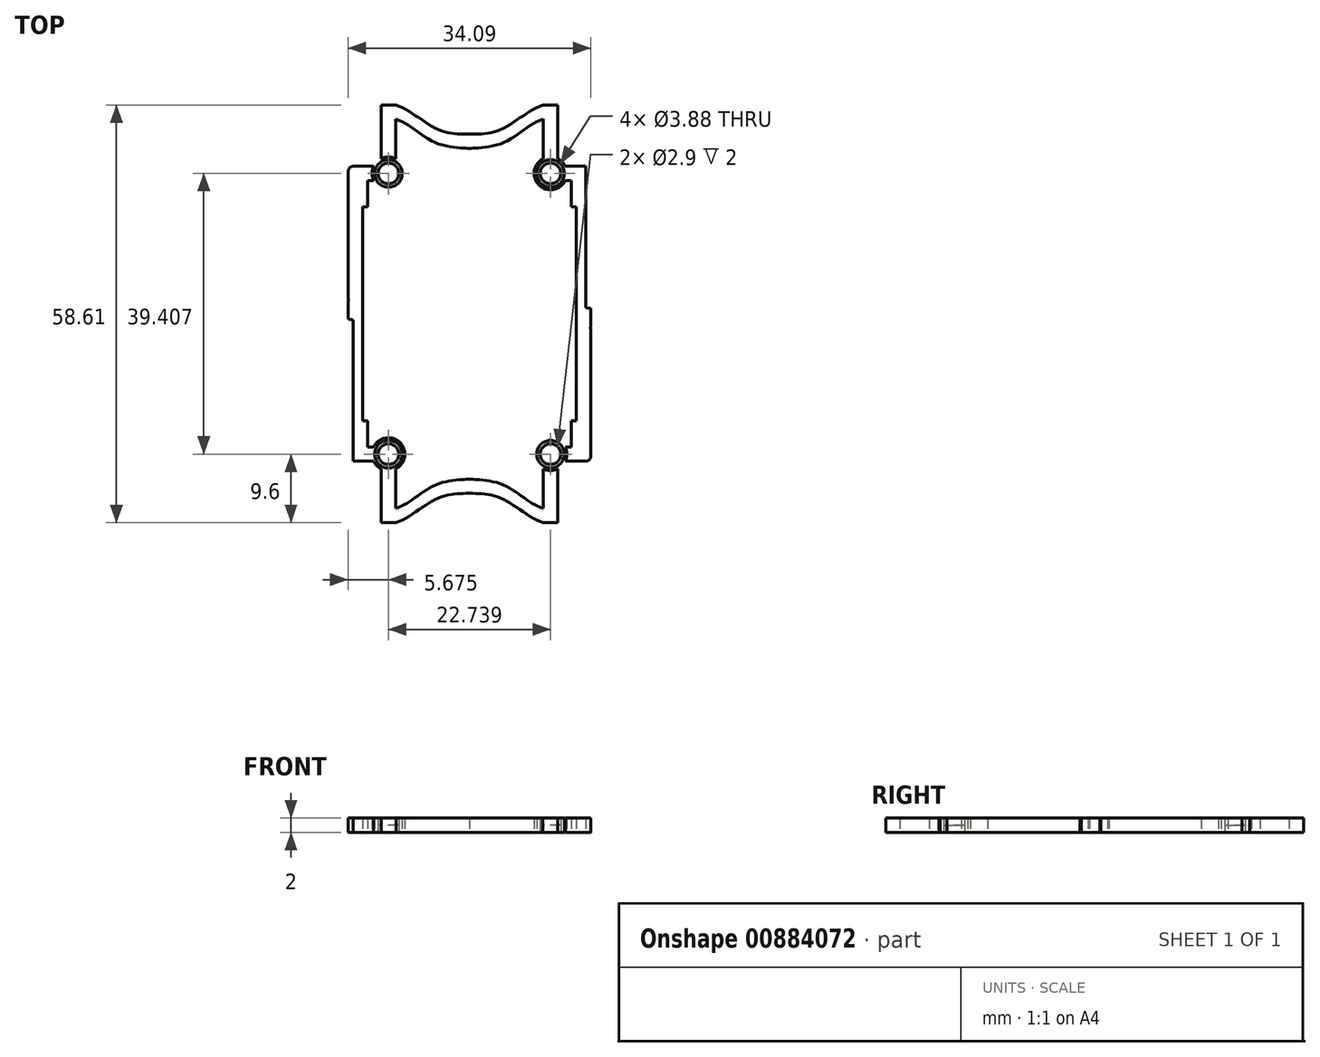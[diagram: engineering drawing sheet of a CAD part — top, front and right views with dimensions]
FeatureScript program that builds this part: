
annotation { "Feature Type Name" : "Feature", "Feature Type Description" : "" }
export const myFeature = defineFeature(function(context is Context, id is Id, definition is map)
    precondition{}
    {
        {
            var Q0;
            Q0=qCreatedBy(makeId("Right.planeOp"),FACE);
            cPlane(context, id + "F0", {"entities" : qUnion([Q0]), "cplaneType" : CPlaneType.OFFSET, "offset" : 33.58 * mm, "width" : 150 * mm, "height" : 150 * mm});
        }
        {
            var Q0;
            Q0=qCreatedBy(makeId("Top.planeOp"),FACE);
            var sketch = newSketch(context, id + "F1", { "sketchPlane" : qUnion([Q0])});
            skLineSegment(sketch, "E0.bottom", {"start": v(17.3, 63.43) * mm, "end": v(23.3, 63.43) * mm});
            skLineSegment(sketch, "E0.top", {"start": v(20.3, 4.82) * mm, "end": v(23.3, 4.82) * mm});
            skLineSegment(sketch, "E0.left", {"start": v(17.3, 63.43) * mm, "end": v(17.3, 38.95) * mm});
            skFitSpline(sketch, "E1", {"points": [v(49.88, 63.43) * mm, v(43.88, 63.43) * mm, v(38.18, 60.08) * mm, v(33.58, 59.34) * mm], "startDerivative": vector(-19.72, 0) * mm, "endDerivative": vector(-14.92, -0.07) * mm});
            skFitSpline(sketch, "E2.MirrorCS", {"points": [v(17.3, 63.43) * mm, v(23.3, 63.43) * mm, v(28.98, 60.08) * mm, v(33.58, 59.34) * mm], "startDerivative": vector(19.72, 0) * mm, "endDerivative": vector(14.92, -0.07) * mm});
            skFitSpline(sketch, "E3.MirrorCS", {"points": [v(49.88, 4.82) * mm, v(43.88, 4.82) * mm, v(38.18, 8.17) * mm, v(33.58, 8.91) * mm], "startDerivative": vector(-19.72, 0) * mm, "endDerivative": vector(-14.92, 0.07) * mm});
            skFitSpline(sketch, "E4.MirrorCS", {"points": [v(17.3, 4.82) * mm, v(23.3, 4.82) * mm, v(28.98, 8.17) * mm, v(33.58, 8.91) * mm], "startDerivative": vector(19.72, 0) * mm, "endDerivative": vector(14.92, 0.07) * mm});
            skLineSegment(sketch, "E5.trimOffspring", {"start": v(43.88, 63.43) * mm, "end": v(49.88, 63.43) * mm});
            skLineSegment(sketch, "E6.trimOffspring", {"start": v(43.88, 4.82) * mm, "end": v(49.88, 4.82) * mm});
            skArc(sketch, "E7.filletArc", {"start": v(17.3, 7.82) * mm, "mid": v(18.17, 5.7) * mm, "end": v(20.3, 4.82) * mm});
            skArc(sketch, "E8.MirrorCS", {"start": v(49.88, 7.82) * mm, "mid": v(49, 5.7) * mm, "end": v(46.88, 4.82) * mm});
            skArc(sketch, "E9.MirrorCS", {"start": v(49.88, 60.43) * mm, "mid": v(49, 62.55) * mm, "end": v(46.88, 63.43) * mm});
            skArc(sketch, "E10.MirrorCS", {"start": v(17.3, 60.43) * mm, "mid": v(18.17, 62.55) * mm, "end": v(20.3, 63.43) * mm});
            skCircle(sketch, "E11", {"center": v(22.21, 53.83) * mm, "radius": 1.45 * mm});
            skFitSpline(sketch, "E12", {"points": [v(17.3, 38.95) * mm, v(17.99, 35.94) * mm, v(16.48, 34.87) * mm], "startDerivative": vector(3.54, -6.71) * mm, "endDerivative": vector(-7.62, -0.35) * mm});
            skLineSegment(sketch, "E13", {"start": v(15.53, 36.16) * mm, "end": v(15.08, 36.16) * mm});
            skLineSegment(sketch, "E14", {"start": v(15.08, 36.16) * mm, "end": v(15.08, 34.12) * mm});
            skLineSegment(sketch, "E15.MirrorCS", {"start": v(15.08, 32.08) * mm, "end": v(15.08, 34.12) * mm});
            skLineSegment(sketch, "E16.MirrorCS", {"start": v(15.53, 32.08) * mm, "end": v(15.08, 32.08) * mm});
            skFitSpline(sketch, "E17.MirrorCS", {"points": [v(17.3, 29.3) * mm, v(17.99, 32.31) * mm, v(16.48, 33.38) * mm], "startDerivative": vector(3.54, 6.71) * mm, "endDerivative": vector(-7.62, 0.35) * mm});
            skLineSegment(sketch, "E18", {"start": v(15.53, 36.16) * mm, "end": v(16.63, 36.16) * mm});
            skFitSpline(sketch, "E19", {"points": [v(16.63, 36.16) * mm, v(16, 35.52) * mm, v(16.48, 34.87) * mm], "startDerivative": vector(0.5, -1.03) * mm, "endDerivative": vector(3.51, -0.24) * mm});
            skFitSpline(sketch, "E20.MirrorCS", {"points": [v(16.63, 32.08) * mm, v(16, 32.73) * mm, v(16.48, 33.38) * mm], "startDerivative": vector(0.5, 1.03) * mm, "endDerivative": vector(3.51, 0.24) * mm});
            skLineSegment(sketch, "E21.MirrorCS", {"start": v(15.53, 32.08) * mm, "end": v(16.63, 32.08) * mm});
            skPoint(sketch, "E22.orphan", {"position": v(15.53, 32.08) * mm});
            skLineSegment(sketch, "E23.trimOffspring", {"start": v(17.3, 29.3) * mm, "end": v(17.3, 7.82) * mm});
            skFitSpline(sketch, "E24.MirrorCS", {"points": [v(49.88, 38.95) * mm, v(49.18, 35.94) * mm, v(50.68, 34.87) * mm], "startDerivative": vector(-3.54, -6.71) * mm, "endDerivative": vector(7.62, -0.35) * mm});
            skFitSpline(sketch, "E25.MirrorCS", {"points": [v(49.88, 29.3) * mm, v(49.18, 32.31) * mm, v(50.68, 33.38) * mm], "startDerivative": vector(-3.54, 6.71) * mm, "endDerivative": vector(7.62, 0.35) * mm});
            skFitSpline(sketch, "E26.MirrorCS", {"points": [v(50.54, 32.08) * mm, v(51.16, 32.73) * mm, v(50.68, 33.38) * mm], "startDerivative": vector(-0.5, 1.03) * mm, "endDerivative": vector(-3.51, 0.24) * mm});
            skFitSpline(sketch, "E27.MirrorCS", {"points": [v(50.54, 36.16) * mm, v(51.16, 35.52) * mm, v(50.68, 34.87) * mm], "startDerivative": vector(-0.5, -1.03) * mm, "endDerivative": vector(-3.51, -0.24) * mm});
            skLineSegment(sketch, "E28.MirrorCS", {"start": v(51.64, 36.16) * mm, "end": v(50.54, 36.16) * mm});
            skLineSegment(sketch, "E29.MirrorCS", {"start": v(51.64, 36.16) * mm, "end": v(52.08, 36.16) * mm});
            skLineSegment(sketch, "E30.MirrorCS", {"start": v(51.64, 32.08) * mm, "end": v(50.54, 32.08) * mm});
            skLineSegment(sketch, "E31.MirrorCS", {"start": v(51.64, 32.08) * mm, "end": v(52.08, 32.08) * mm});
            skLineSegment(sketch, "E32.MirrorCS", {"start": v(52.08, 32.08) * mm, "end": v(52.08, 34.12) * mm});
            skLineSegment(sketch, "E33.MirrorCS", {"start": v(52.08, 36.16) * mm, "end": v(52.08, 34.12) * mm});
            skLineSegment(sketch, "E34", {"start": v(49.88, 60.43) * mm, "end": v(49.88, 38.95) * mm});
            skLineSegment(sketch, "E35", {"start": v(49.88, 29.3) * mm, "end": v(49.88, 7.82) * mm});
            skCircle(sketch, "E36.MirrorC", {"center": v(44.95, 53.83) * mm, "radius": 1.45 * mm});
            skLineSegment(sketch, "E37", {"start": v(33.58, 59.34) * mm, "end": v(33.58, 8.91) * mm});
            skLineSegment(sketch, "E38", {"start": v(15.08, 34.12) * mm, "end": v(52.08, 34.12) * mm});
            skCircle(sketch, "E39.MirrorC", {"center": v(22.21, 14.42) * mm, "radius": 1.45 * mm});
            skCircle(sketch, "E40.MirrorC", {"center": v(44.95, 14.42) * mm, "radius": 1.45 * mm});
            skCircle(sketch, "E41", {"center": v(22.21, 14.42) * mm, "radius": 1.94 * mm});
            skCircle(sketch, "E42", {"center": v(22.21, 14.42) * mm, "radius": 2.3 * mm});
            skCircle(sketch, "E43.MirrorC", {"center": v(22.21, 53.83) * mm, "radius": 1.94 * mm});
            skCircle(sketch, "E44.MirrorC", {"center": v(22.21, 53.83) * mm, "radius": 2.3 * mm});
            skCircle(sketch, "E45.MirrorC", {"center": v(44.95, 14.42) * mm, "radius": 2.3 * mm});
            skCircle(sketch, "E46.MirrorC", {"center": v(44.95, 14.42) * mm, "radius": 1.94 * mm});
            skCircle(sketch, "E47.MirrorC", {"center": v(44.95, 53.83) * mm, "radius": 2.3 * mm});
            skCircle(sketch, "E48.MirrorC", {"center": v(44.95, 53.83) * mm, "radius": 1.94 * mm});
            skLineSegment(sketch, "E49", {"start": v(19.91, 14.42) * mm, "end": v(17.3, 14.42) * mm});
            skLineSegment(sketch, "E50", {"start": v(22.21, 12.12) * mm, "end": v(22.21, 4.82) * mm});
            skLineSegment(sketch, "E51", {"start": v(23.21, 12.35) * mm, "end": v(23.21, 4.82) * mm});
            skLineSegment(sketch, "E52.MirrorCS", {"start": v(21.21, 12.35) * mm, "end": v(21.21, 4.82) * mm});
            skLineSegment(sketch, "E53", {"start": v(20.14, 13.42) * mm, "end": v(17.3, 13.42) * mm});
            skLineSegment(sketch, "E54.MirrorCS", {"start": v(20.14, 15.42) * mm, "end": v(17.3, 15.42) * mm});
            skLineSegment(sketch, "E55.MirrorCS", {"start": v(20.14, 52.83) * mm, "end": v(17.3, 52.83) * mm});
            skLineSegment(sketch, "E56.MirrorCS", {"start": v(20.14, 54.83) * mm, "end": v(17.3, 54.83) * mm});
            skLineSegment(sketch, "E57.MirrorCS", {"start": v(21.21, 55.9) * mm, "end": v(21.21, 63.43) * mm});
            skLineSegment(sketch, "E58.MirrorCS", {"start": v(23.21, 55.9) * mm, "end": v(23.21, 63.43) * mm});
            skLineSegment(sketch, "E59.MirrorCS", {"start": v(43.95, 55.9) * mm, "end": v(43.95, 63.43) * mm});
            skLineSegment(sketch, "E60.MirrorCS", {"start": v(45.95, 55.9) * mm, "end": v(45.95, 63.43) * mm});
            skLineSegment(sketch, "E61.MirrorCS", {"start": v(47.03, 54.83) * mm, "end": v(49.88, 54.83) * mm});
            skLineSegment(sketch, "E62.MirrorCS", {"start": v(47.03, 52.83) * mm, "end": v(49.88, 52.83) * mm});
            skLineSegment(sketch, "E63.MirrorCS", {"start": v(47.03, 15.42) * mm, "end": v(49.88, 15.42) * mm});
            skLineSegment(sketch, "E64.MirrorCS", {"start": v(47.03, 13.42) * mm, "end": v(49.88, 13.42) * mm});
            skLineSegment(sketch, "E65.MirrorCS", {"start": v(43.95, 12.35) * mm, "end": v(43.95, 4.82) * mm});
            skLineSegment(sketch, "E66.MirrorCS", {"start": v(45.95, 12.35) * mm, "end": v(45.95, 4.82) * mm});
            skLineSegment(sketch, "E67", {"start": v(19.3, 52.83) * mm, "end": v(19.3, 49.12) * mm});
            skLineSegment(sketch, "E68.MirrorCS", {"start": v(47.88, 52.83) * mm, "end": v(47.88, 49.12) * mm});
            skFitSpline(sketch, "E69", {"points": [v(23.21, 61.43) * mm, v(28.98, 58.08) * mm, v(33.58, 57.34) * mm], "startDerivative": vector(11.37, -3.22) * mm, "endDerivative": vector(3.8, -0.38) * mm});
            skFitSpline(sketch, "E70.MirrorCS", {"points": [v(43.95, 61.43) * mm, v(38.18, 58.08) * mm, v(33.58, 57.34) * mm], "startDerivative": vector(-11.37, -3.22) * mm, "endDerivative": vector(-3.8, -0.38) * mm});
            skFitSpline(sketch, "E71.MirrorCS", {"points": [v(43.95, 6.82) * mm, v(38.18, 10.17) * mm, v(33.58, 10.91) * mm], "startDerivative": vector(-11.37, 3.22) * mm, "endDerivative": vector(-3.8, 0.38) * mm});
            skLineSegment(sketch, "E72.MirrorCS", {"start": v(33.58, 8.91) * mm, "end": v(33.58, 59.34) * mm});
            skFitSpline(sketch, "E73.MirrorCS", {"points": [v(23.21, 6.82) * mm, v(28.98, 10.17) * mm, v(33.58, 10.91) * mm], "startDerivative": vector(11.37, 3.22) * mm, "endDerivative": vector(3.8, 0.38) * mm});
            skLineSegment(sketch, "E74", {"start": v(17.3, 38.95) * mm, "end": v(17.3, 29.3) * mm});
            skLineSegment(sketch, "E75", {"start": v(49.88, 38.95) * mm, "end": v(49.88, 29.3) * mm});
            skLineSegment(sketch, "E76.bottom", {"start": v(18.58, 49.12) * mm, "end": v(19.3, 49.12) * mm});
            skLineSegment(sketch, "E76.left", {"start": v(18.58, 49.12) * mm, "end": v(18.58, 19.12) * mm});
            skLineSegment(sketch, "E76.right", {"start": v(48.58, 49.12) * mm, "end": v(48.58, 19.12) * mm});
            skPoint(sketch, "E76.middle", {"position": v(33.58, 34.12) * mm});
            skLineSegment(sketch, "E77", {"start": v(17.3, 54.83) * mm, "end": v(17.3, 54.83) * mm});
            skLineSegment(sketch, "E78", {"start": v(16.54, 54.08) * mm, "end": v(16.54, 34.12) * mm});
            skLineSegment(sketch, "E79.MirrorCS", {"start": v(50.63, 54.08) * mm, "end": v(50.63, 34.12) * mm});
            skLineSegment(sketch, "E80.MirrorCS", {"start": v(16.54, 14.17) * mm, "end": v(16.54, 34.12) * mm});
            skLineSegment(sketch, "E81.MirrorCS", {"start": v(50.63, 14.17) * mm, "end": v(50.63, 34.12) * mm});
            skPoint(sketch, "E82.visualSharp", {"position": v(16.54, 54.83) * mm});
            skArc(sketch, "E82.filletArc", {"start": v(17.3, 54.83) * mm, "mid": v(16.76, 54.6) * mm, "end": v(16.54, 54.08) * mm});
            skPoint(sketch, "E83.orphan", {"position": v(19.3, 15.42) * mm});
            skLineSegment(sketch, "E84.trimOffspring", {"start": v(47.88, 49.12) * mm, "end": v(48.58, 49.12) * mm});
            skPoint(sketch, "E85.trimOffspring.end.orphan", {"position": v(47.88, 15.42) * mm});
            skLineSegment(sketch, "E86.MirrorCS", {"start": v(47.88, 19.12) * mm, "end": v(48.58, 19.12) * mm});
            skLineSegment(sketch, "E87.MirrorCS", {"start": v(47.88, 15.42) * mm, "end": v(47.88, 19.12) * mm});
            skLineSegment(sketch, "E88.MirrorCS", {"start": v(18.58, 19.12) * mm, "end": v(19.3, 19.12) * mm});
            skLineSegment(sketch, "E89.MirrorCS", {"start": v(19.3, 15.42) * mm, "end": v(19.3, 19.12) * mm});
            skLineSegment(sketch, "E90.bottom", {"start": v(18.58, 49.12) * mm, "end": v(48.58, 49.12) * mm});
            skLineSegment(sketch, "E90.top", {"start": v(18.58, 19.12) * mm, "end": v(48.58, 19.12) * mm});
            skPoint(sketch, "E91", {"position": v(24.33, 10.91) * mm});
            skPoint(sketch, "E92", {"position": v(42.83, 10.91) * mm});
            skLineSegment(sketch, "E93", {"start": v(24.33, 10.91) * mm, "end": v(24.33, 7.27) * mm});
            skLineSegment(sketch, "E94.MirrorCS", {"start": v(42.83, 10.91) * mm, "end": v(42.83, 7.27) * mm});
            skPoint(sketch, "E95.MirrorP", {"position": v(16.54, 13.42) * mm});
            skArc(sketch, "E96.MirrorCS", {"start": v(17.3, 13.42) * mm, "mid": v(16.76, 13.64) * mm, "end": v(16.54, 14.17) * mm});
            skArc(sketch, "E97.MirrorCS", {"start": v(49.88, 13.42) * mm, "mid": v(50.4, 13.64) * mm, "end": v(50.63, 14.17) * mm});
            skArc(sketch, "E98.MirrorCS", {"start": v(49.88, 54.83) * mm, "mid": v(50.4, 54.6) * mm, "end": v(50.63, 54.08) * mm});
            skPoint(sketch, "E99.MirrorCS.end.orphan", {"position": v(50.63, 54.83) * mm});
            skPoint(sketch, "E99.MirrorCS.start.orphan", {"position": v(49.88, 54.83) * mm});
            skPoint(sketch, "E100.orphan", {"position": v(50.63, 13.42) * mm});
            skPoint(sketch, "E101.MirrorCS.start.orphan", {"position": v(49.88, 13.42) * mm});
            skPoint(sketch, "E102.MirrorCS.start.orphan", {"position": v(17.3, 13.42) * mm});
            skSolve(sketch);
        }
        {
            var Q0;
            {var subQ0=sQuery(id+"F1.wireOp",EDGE,"E74");var subQ9=sQuery(id+"F1.wireOp",EDGE,"E38");var subQ10=makeQuery(id+"F1.imprint","INTERSECT",VERTEX,{"derivedFrom":[subQ9,subQ0]});Q0=makeQuery(id+"F1.imprint","IMPRINT",FACE,{"disambiguationData":[TD([[makeQuery(id+"F1.imprint","IMPRINT",EDGE,{"disambiguationData":[TD([[subQ10,-1.0]])],"derivedFrom":subQ9}),1.0]])]});}
            var Q1;
            {var subQ6=sQuery(id+"F1.wireOp",EDGE,"E56.MirrorCS");Q1=makeQuery(id+"F1.imprint","IMPRINT",FACE,{"disambiguationData":[TD([[makeQuery(id+"F1.imprint","IMPRINT",EDGE,{"derivedFrom":subQ6}),1.0]])]});}
            var Q2;
            {var subQ4=sQuery(id+"F1.wireOp",EDGE,"E57.MirrorCS");Q2=makeQuery(id+"F1.imprint","IMPRINT",FACE,{"disambiguationData":[TD([[makeQuery(id+"F1.imprint","IMPRINT",EDGE,{"derivedFrom":subQ4}),-1.0]])]});}
            var Q3;
            {var subQ0=sQuery(id+"F1.wireOp",EDGE,"E69");Q3=makeQuery(id+"F1.imprint","IMPRINT",FACE,{"disambiguationData":[TD([[makeQuery(id+"F1.imprint","IMPRINT",EDGE,{"derivedFrom":subQ0}),1.0]])]});}
            var Q4;
            {var subQ3=sQuery(id+"F1.wireOp",EDGE,"E70.MirrorCS");Q4=makeQuery(id+"F1.imprint","IMPRINT",FACE,{"disambiguationData":[TD([[makeQuery(id+"F1.imprint","IMPRINT",EDGE,{"derivedFrom":subQ3}),-1.0]])]});}
            var Q5;
            {var subQ6=sQuery(id+"F1.wireOp",EDGE,"E60.MirrorCS");Q5=makeQuery(id+"F1.imprint","IMPRINT",FACE,{"disambiguationData":[TD([[makeQuery(id+"F1.imprint","IMPRINT",EDGE,{"derivedFrom":subQ6}),1.0]])]});}
            var Q6;
            {var subQ4=sQuery(id+"F1.wireOp",EDGE,"E61.MirrorCS");var subQ6=sQuery(id+"F1.wireOp",EDGE,"E34");var subQ7=makeQuery(id+"F1.imprint","INTERSECT",VERTEX,{"derivedFrom":[subQ6,subQ4]});Q6=makeQuery(id+"F1.imprint","IMPRINT",FACE,{"disambiguationData":[TD([[makeQuery(id+"F1.imprint","IMPRINT",EDGE,{"disambiguationData":[TD([[subQ7,-1.0]])],"derivedFrom":subQ6}),-1.0]])]});}
            var Q7;
            {var subQ0=sQuery(id+"F1.wireOp",EDGE,"E63.MirrorCS");var subQ2=sQuery(id+"F1.wireOp",EDGE,"E35");var subQ3=makeQuery(id+"F1.imprint","INTERSECT",VERTEX,{"derivedFrom":[subQ2,subQ0]});Q7=makeQuery(id+"F1.imprint","IMPRINT",FACE,{"disambiguationData":[TD([[makeQuery(id+"F1.imprint","IMPRINT",EDGE,{"disambiguationData":[TD([[subQ3,-1.0]])],"derivedFrom":subQ2}),-1.0]])]});}
            var Q8;
            {var subQ4=sQuery(id+"F1.wireOp",EDGE,"E66.MirrorCS");Q8=makeQuery(id+"F1.imprint","IMPRINT",FACE,{"disambiguationData":[TD([[makeQuery(id+"F1.imprint","IMPRINT",EDGE,{"derivedFrom":subQ4}),-1.0]])]});}
            var Q9;
            {var subQ0=sQuery(id+"F1.wireOp",EDGE,"E71.MirrorCS");Q9=makeQuery(id+"F1.imprint","IMPRINT",FACE,{"disambiguationData":[TD([[makeQuery(id+"F1.imprint","IMPRINT",EDGE,{"derivedFrom":subQ0}),1.0]])]});}
            var Q10;
            {var subQ3=sQuery(id+"F1.wireOp",EDGE,"E73.MirrorCS");Q10=makeQuery(id+"F1.imprint","IMPRINT",FACE,{"disambiguationData":[TD([[makeQuery(id+"F1.imprint","IMPRINT",EDGE,{"derivedFrom":subQ3}),-1.0]])]});}
            var Q11;
            {var subQ0=sQuery(id+"F1.wireOp",EDGE,"E50");Q11=makeQuery(id+"F1.imprint","IMPRINT",FACE,{"disambiguationData":[TD([[makeQuery(id+"F1.imprint","IMPRINT",EDGE,{"derivedFrom":subQ0}),1.0]])]});}
            var Q12;
            {var subQ0=sQuery(id+"F1.wireOp",EDGE,"E50");Q12=makeQuery(id+"F1.imprint","IMPRINT",FACE,{"disambiguationData":[TD([[makeQuery(id+"F1.imprint","IMPRINT",EDGE,{"derivedFrom":subQ0}),-1.0]])]});}
            var Q13;
            {var subQ0=sQuery(id+"F1.wireOp",EDGE,"E49");Q13=makeQuery(id+"F1.imprint","IMPRINT",FACE,{"disambiguationData":[TD([[makeQuery(id+"F1.imprint","IMPRINT",EDGE,{"derivedFrom":subQ0}),1.0]])]});}
            var Q14;
            {var subQ0=sQuery(id+"F1.wireOp",EDGE,"E49");Q14=makeQuery(id+"F1.imprint","IMPRINT",FACE,{"disambiguationData":[TD([[makeQuery(id+"F1.imprint","IMPRINT",EDGE,{"derivedFrom":subQ0}),-1.0]])]});}
            var Q15;
            {var subQ5=sQuery(id+"F1.wireOp",EDGE,"E74");var subQ8=sQuery(id+"F1.wireOp",EDGE,"E38");var subQ9=makeQuery(id+"F1.imprint","INTERSECT",VERTEX,{"derivedFrom":[subQ8,subQ5]});Q15=makeQuery(id+"F1.imprint","IMPRINT",FACE,{"disambiguationData":[TD([[makeQuery(id+"F1.imprint","IMPRINT",EDGE,{"disambiguationData":[TD([[subQ9,-1.0]])],"derivedFrom":subQ8}),-1.0]])]});}
            var Q16;
            Q16=makeQuery(id+"F1.imprint","IMPRINT",FACE,{"disambiguationData":[TD([[makeQuery(id+"F1.imprint","IMPRINT",EDGE,{"derivedFrom":sQuery(id+"F1.wireOp",EDGE,"E43.MirrorC")}),1.0]])]});
            var Q17;
            Q17=makeQuery(id+"F1.imprint","IMPRINT",FACE,{"disambiguationData":[TD([[makeQuery(id+"F1.imprint","IMPRINT",EDGE,{"derivedFrom":sQuery(id+"F1.wireOp",EDGE,"E48.MirrorC")}),-1.0]])]});
            var Q18;
            Q18=makeQuery(id+"F1.imprint","IMPRINT",FACE,{"disambiguationData":[TD([[makeQuery(id+"F1.imprint","IMPRINT",EDGE,{"derivedFrom":sQuery(id+"F1.wireOp",EDGE,"E41")}),-1.0]])]});
            var Q19;
            Q19=makeQuery(id+"F1.imprint","IMPRINT",FACE,{"disambiguationData":[TD([[makeQuery(id+"F1.imprint","IMPRINT",EDGE,{"derivedFrom":sQuery(id+"F1.wireOp",EDGE,"E46.MirrorC")}),1.0]])]});
            var Q20;
            {var subQ0=sQuery(id+"F1.wireOp",EDGE,"E76.right");var subQ1=sQuery(id+"F1.wireOp",EDGE,"E38");var subQ2=makeQuery(id+"F1.imprint","INTERSECT",VERTEX,{"derivedFrom":[subQ1,subQ0]});Q20=makeQuery(id+"F1.imprint","IMPRINT",FACE,{"disambiguationData":[TD([[makeQuery(id+"F1.imprint","IMPRINT",EDGE,{"disambiguationData":[TD([[subQ2,-1.0]])],"derivedFrom":subQ1}),-1.0]])]});}
            var Q21;
            {var subQ6=sQuery(id+"F1.wireOp",EDGE,"E76.right");var subQ7=sQuery(id+"F1.wireOp",EDGE,"E38");var subQ8=makeQuery(id+"F1.imprint","INTERSECT",VERTEX,{"derivedFrom":[subQ7,subQ6]});Q21=makeQuery(id+"F1.imprint","IMPRINT",FACE,{"disambiguationData":[TD([[makeQuery(id+"F1.imprint","IMPRINT",EDGE,{"disambiguationData":[TD([[subQ8,-1.0]])],"derivedFrom":subQ7}),1.0]])]});}
            var Q22;
            {var subQ5=sQuery(id+"F1.wireOp",EDGE,"E101.MirrorCS");Q22=makeQuery(id+"F1.imprint","IMPRINT",FACE,{"disambiguationData":[TD([[makeQuery(id+"F1.imprint","IMPRINT",EDGE,{"derivedFrom":subQ5}),1.0]])]});}
            var Q23;
            {var subQ0=sQuery(id+"F1.wireOp",EDGE,"E75");var subQ1=sQuery(id+"F1.wireOp",EDGE,"E25.MirrorCS");var subQ3=makeQuery(id+"F1.imprint","INTERSECT",VERTEX,{"derivedFrom":[subQ1,subQ0]});Q23=makeQuery(id+"F1.imprint","IMPRINT",FACE,{"disambiguationData":[TD([[makeQuery(id+"F1.imprint","IMPRINT",EDGE,{"disambiguationData":[TD([[subQ3,1.0]])],"derivedFrom":subQ1}),-1.0]])]});}
            var Q24;
            {var subQ9=sQuery(id+"F1.wireOp",EDGE,"E99.MirrorCS");Q24=makeQuery(id+"F1.imprint","IMPRINT",FACE,{"disambiguationData":[TD([[makeQuery(id+"F1.imprint","IMPRINT",EDGE,{"derivedFrom":subQ9}),-1.0]])]});}
            var Q25;
            {var subQ0=sQuery(id+"F1.wireOp",EDGE,"E75");var subQ1=sQuery(id+"F1.wireOp",EDGE,"E24.MirrorCS");var subQ3=makeQuery(id+"F1.imprint","INTERSECT",VERTEX,{"derivedFrom":[subQ1,subQ0]});Q25=makeQuery(id+"F1.imprint","IMPRINT",FACE,{"disambiguationData":[TD([[makeQuery(id+"F1.imprint","IMPRINT",EDGE,{"disambiguationData":[TD([[subQ3,1.0]])],"derivedFrom":subQ1}),1.0]])]});}
            var Q26;
            {var subQ0=sQuery(id+"F1.wireOp",EDGE,"E75");var subQ1=sQuery(id+"F1.wireOp",EDGE,"E24.MirrorCS");var subQ2=makeQuery(id+"F1.imprint","INTERSECT",VERTEX,{"derivedFrom":[subQ1,subQ0]});Q26=makeQuery(id+"F1.imprint","IMPRINT",FACE,{"disambiguationData":[TD([[makeQuery(id+"F1.imprint","IMPRINT",EDGE,{"disambiguationData":[TD([[subQ2,-1.0]])],"derivedFrom":subQ1}),-1.0]])]});}
            var Q27;
            {var subQ0=sQuery(id+"F1.wireOp",EDGE,"E75");var subQ1=sQuery(id+"F1.wireOp",EDGE,"E25.MirrorCS");var subQ2=makeQuery(id+"F1.imprint","INTERSECT",VERTEX,{"derivedFrom":[subQ1,subQ0]});Q27=makeQuery(id+"F1.imprint","IMPRINT",FACE,{"disambiguationData":[TD([[makeQuery(id+"F1.imprint","IMPRINT",EDGE,{"disambiguationData":[TD([[subQ2,-1.0]])],"derivedFrom":subQ1}),1.0]])]});}
            var Q28;
            {var subQ13=sQuery(id+"F1.wireOp",EDGE,"E77");Q28=makeQuery(id+"F1.imprint","IMPRINT",FACE,{"disambiguationData":[TD([[makeQuery(id+"F1.imprint","IMPRINT",EDGE,{"derivedFrom":subQ13}),1.0]])]});}
            var Q29;
            {var subQ0=sQuery(id+"F1.wireOp",EDGE,"E74");var subQ1=sQuery(id+"F1.wireOp",EDGE,"E12");var subQ3=makeQuery(id+"F1.imprint","INTERSECT",VERTEX,{"derivedFrom":[subQ1,subQ0]});Q29=makeQuery(id+"F1.imprint","IMPRINT",FACE,{"disambiguationData":[TD([[makeQuery(id+"F1.imprint","IMPRINT",EDGE,{"disambiguationData":[TD([[subQ3,1.0]])],"derivedFrom":subQ1}),-1.0]])]});}
            var Q30;
            {var subQ0=sQuery(id+"F1.wireOp",EDGE,"E74");var subQ1=sQuery(id+"F1.wireOp",EDGE,"E17.MirrorCS");var subQ3=makeQuery(id+"F1.imprint","INTERSECT",VERTEX,{"derivedFrom":[subQ1,subQ0]});Q30=makeQuery(id+"F1.imprint","IMPRINT",FACE,{"disambiguationData":[TD([[makeQuery(id+"F1.imprint","IMPRINT",EDGE,{"disambiguationData":[TD([[subQ3,1.0]])],"derivedFrom":subQ1}),1.0]])]});}
            var Q31;
            {var subQ14=sQuery(id+"F1.wireOp",EDGE,"E102.MirrorCS");Q31=makeQuery(id+"F1.imprint","IMPRINT",FACE,{"disambiguationData":[TD([[makeQuery(id+"F1.imprint","IMPRINT",EDGE,{"derivedFrom":subQ14}),-1.0]])]});}
            var Q32;
            {var subQ0=sQuery(id+"F1.wireOp",EDGE,"E74");var subQ1=sQuery(id+"F1.wireOp",EDGE,"E17.MirrorCS");var subQ2=makeQuery(id+"F1.imprint","INTERSECT",VERTEX,{"derivedFrom":[subQ1,subQ0]});Q32=makeQuery(id+"F1.imprint","IMPRINT",FACE,{"disambiguationData":[TD([[makeQuery(id+"F1.imprint","IMPRINT",EDGE,{"disambiguationData":[TD([[subQ2,-1.0]])],"derivedFrom":subQ1}),-1.0]])]});}
            var Q33;
            {var subQ0=sQuery(id+"F1.wireOp",EDGE,"E74");var subQ1=sQuery(id+"F1.wireOp",EDGE,"E12");var subQ2=makeQuery(id+"F1.imprint","INTERSECT",VERTEX,{"derivedFrom":[subQ1,subQ0]});Q33=makeQuery(id+"F1.imprint","IMPRINT",FACE,{"disambiguationData":[TD([[makeQuery(id+"F1.imprint","IMPRINT",EDGE,{"disambiguationData":[TD([[subQ2,-1.0]])],"derivedFrom":subQ1}),1.0]])]});}
            var Q34;
            {var subQ0=sQuery(id+"F1.wireOp",EDGE,"E68.MirrorCS");Q34=makeQuery(id+"F1.imprint","IMPRINT",FACE,{"disambiguationData":[TD([[makeQuery(id+"F1.imprint","IMPRINT",EDGE,{"derivedFrom":subQ0}),1.0]])]});}
            var Q35;
            {var subQ0=sQuery(id+"F1.wireOp",EDGE,"E87.MirrorCS");Q35=makeQuery(id+"F1.imprint","IMPRINT",FACE,{"disambiguationData":[TD([[makeQuery(id+"F1.imprint","IMPRINT",EDGE,{"derivedFrom":subQ0}),-1.0]])]});}
            var Q36;
            {var subQ13=sQuery(id+"F1.wireOp",EDGE,"E82.filletArc");Q36=makeQuery(id+"F1.imprint","IMPRINT",FACE,{"disambiguationData":[TD([[makeQuery(id+"F1.imprint","IMPRINT",EDGE,{"derivedFrom":subQ13}),1.0]])]});}
            var Q37;
            {var subQ15=sQuery(id+"F1.wireOp",EDGE,"E98.MirrorCS");Q37=makeQuery(id+"F1.imprint","IMPRINT",FACE,{"disambiguationData":[TD([[makeQuery(id+"F1.imprint","IMPRINT",EDGE,{"derivedFrom":subQ15}),-1.0]])]});}
            var Q38;
            {var subQ5=sQuery(id+"F1.wireOp",EDGE,"E97.MirrorCS");Q38=makeQuery(id+"F1.imprint","IMPRINT",FACE,{"disambiguationData":[TD([[makeQuery(id+"F1.imprint","IMPRINT",EDGE,{"derivedFrom":subQ5}),1.0]])]});}
            var Q39;
            {var subQ5=sQuery(id+"F1.wireOp",EDGE,"E96.MirrorCS");Q39=makeQuery(id+"F1.imprint","IMPRINT",FACE,{"disambiguationData":[TD([[makeQuery(id+"F1.imprint","IMPRINT",EDGE,{"derivedFrom":subQ5}),-1.0]])]});}
            extrude(context, id + "F2", {"entities" : qUnion([Q0, Q1, Q2, Q3, Q4, Q5, Q6, Q7, Q8, Q9, Q10, Q11, Q12, Q13, Q14, Q15, Q16, Q17, Q18, Q19, Q20, Q21, Q22, Q23, Q24, Q25, Q26, Q27, Q28, Q29, Q30, Q31, Q32, Q33, Q34, Q35, Q36, Q37, Q38, Q39]), "depth" : 2 * mm, "offsetDistance" : 25 * mm});
        }
        {
            var Q0;
            Q0=makeQuery(id+"F1.imprint","IMPRINT",FACE,{"disambiguationData":[TD([[makeQuery(id+"F1.imprint","IMPRINT",EDGE,{"derivedFrom":sQuery(id+"F1.wireOp",EDGE,"E40.MirrorC")}),-1.0]])]});
            var Q1;
            Q1=makeQuery(id+"F1.imprint","IMPRINT",FACE,{"disambiguationData":[TD([[makeQuery(id+"F1.imprint","IMPRINT",EDGE,{"derivedFrom":sQuery(id+"F1.wireOp",EDGE,"E39.MirrorC")}),1.0]])]});
            var Q2;
            Q2=makeQuery(id+"F1.imprint","IMPRINT",FACE,{"disambiguationData":[TD([[makeQuery(id+"F1.imprint","IMPRINT",EDGE,{"derivedFrom":sQuery(id+"F1.wireOp",EDGE,"E36.MirrorC")}),1.0]])]});
            var Q3;
            Q3=makeQuery(id+"F1.imprint","IMPRINT",FACE,{"disambiguationData":[TD([[makeQuery(id+"F1.imprint","IMPRINT",EDGE,{"derivedFrom":sQuery(id+"F1.wireOp",EDGE,"E11")}),-1.0]])]});
            extrude(context, id + "F3", {"entities" : qUnion([Q0, Q1, Q2, Q3]), "operationType" : NewBodyOperationType.ADD, "depth" : 1 * mm, "offsetDistance" : 25 * mm});
        }
    });
